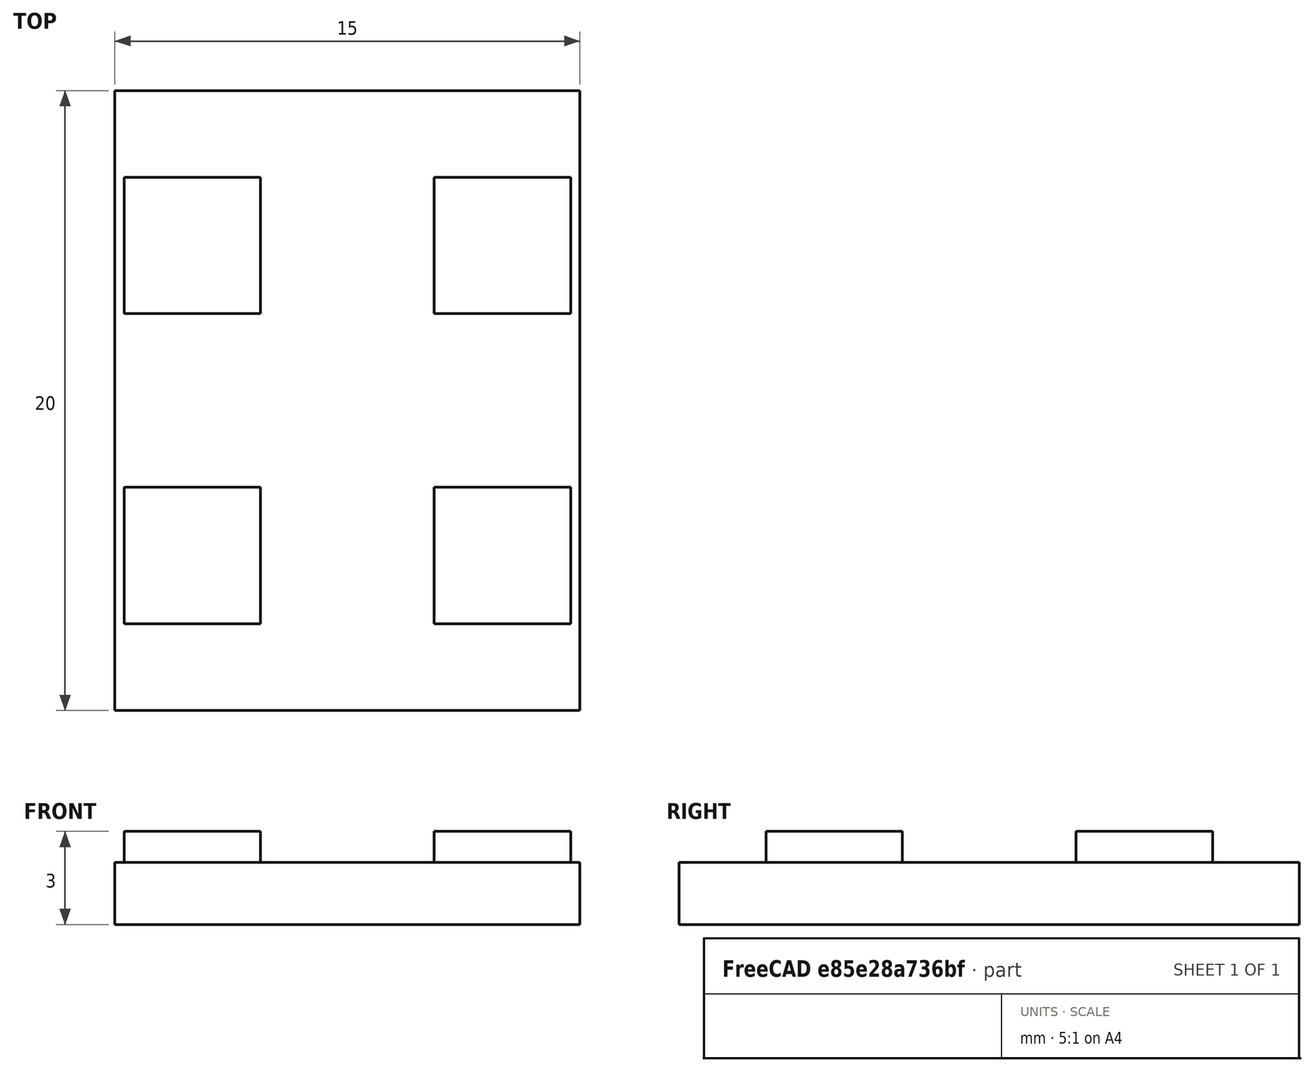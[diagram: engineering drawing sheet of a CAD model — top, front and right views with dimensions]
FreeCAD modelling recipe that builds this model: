
FCSTD DOCUMENT  (FreeCAD 0.18.4R)
Label: floor-junction-v1
License: All rights reserved
LicenseURL: http://en.wikipedia.org/wiki/All_rights_reserved
objects: PartDesign::Pocket×5, Part::Feature×1, PartDesign::FeatureBase×1, PartDesign::Body×1
note: 13 computed .brp shape members not serialized (recipe doc carries the construction recipe); baked Part::Feature solids carry a one-line shape summary decoded from their .brp

FEATURE [Part::Feature] Pad005001  label="Pad006"
  shape: bbox 15 x 20 x 14 mm, 26 faces (baked)
FEATURE [PartDesign::FeatureBase] BaseFeature
  BaseFeature = -> Pad005001
FEATURE [PartDesign::Pocket] Pocket
  BaseFeature = -> BaseFeature
  Length = 3
  Length2 = 100
  Profile = -> BaseFeature [Face18]
  Type = 0
FEATURE [PartDesign::Pocket] Pocket001
  BaseFeature = -> Pocket
  Length = 3
  Length2 = 100
  Profile = -> Pocket [Face24]
  Type = 0
FEATURE [PartDesign::Pocket] Pocket002
  BaseFeature = -> Pocket001
  Length = 3
  Length2 = 100
  Profile = -> Pocket001 [Face23]
  Type = 0
FEATURE [PartDesign::Pocket] Pocket003
  BaseFeature = -> Pocket002
  Length = 3
  Length2 = 100
  Profile = -> Pocket002 [Face26]
  Type = 0
FEATURE [PartDesign::Pocket] Pocket004
  BaseFeature = -> Pocket003
  Length = 8
  Length2 = 100
  Profile = -> Pocket003 [Face2]
  Type = 0
FEATURE [PartDesign::Body] Body
  BaseFeature = -> Pad005001
  Group = -> [BaseFeature,Pocket,Pocket001,Pocket002,Pocket003,Pocket004]
  Origin = -> Origin
  Tip = -> Pocket004
